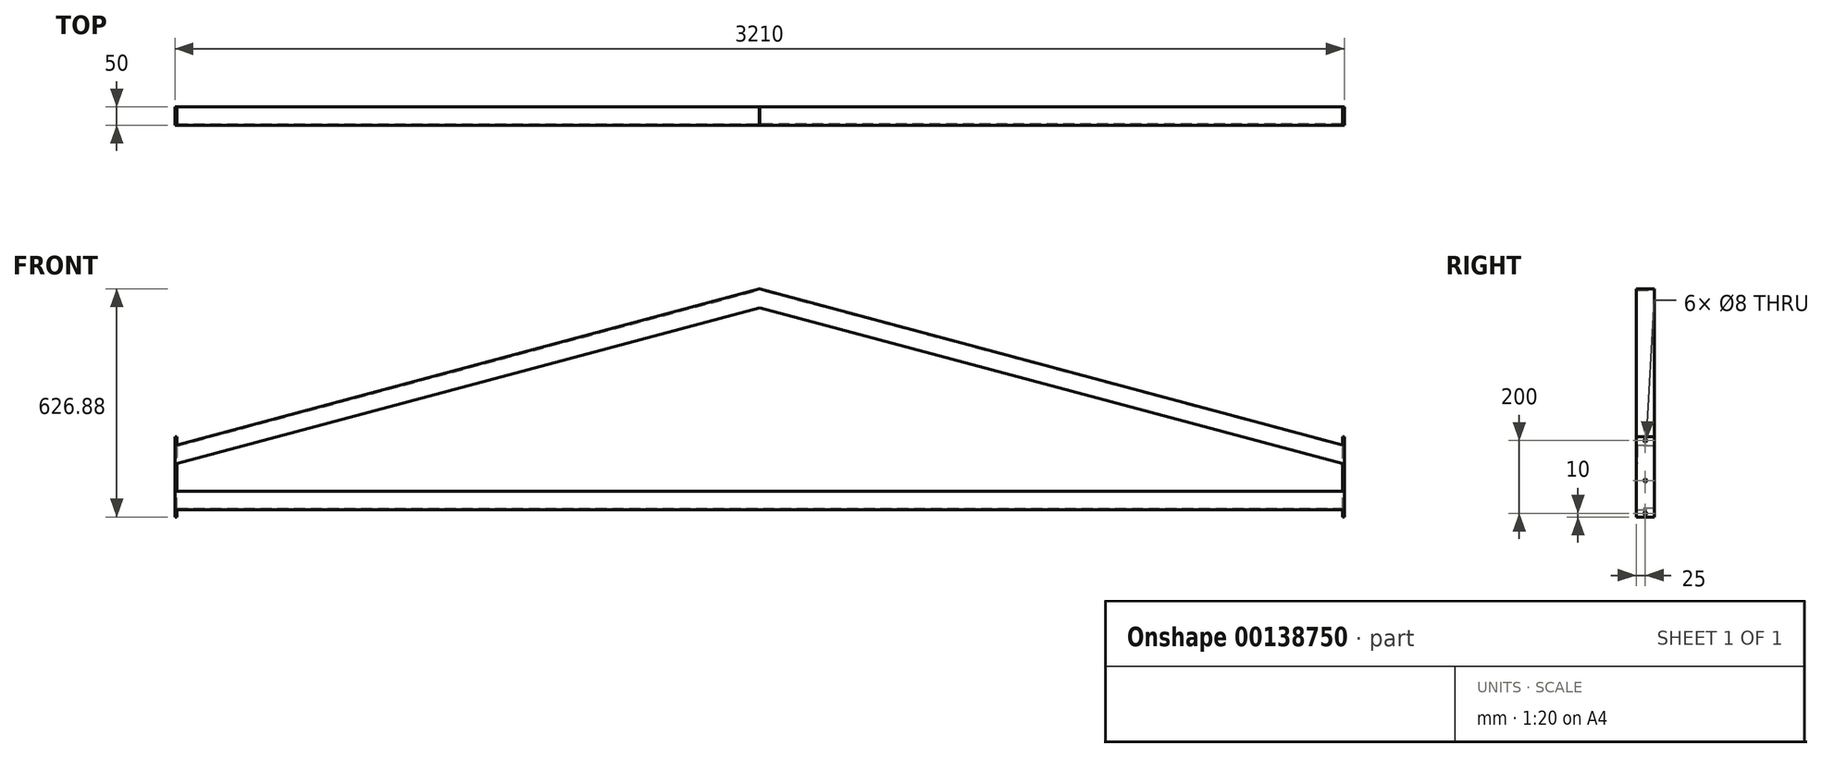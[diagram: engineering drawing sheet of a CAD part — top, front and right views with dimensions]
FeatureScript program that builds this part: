
annotation { "Feature Type Name" : "Feature", "Feature Type Description" : "" }
export const myFeature = defineFeature(function(context is Context, id is Id, definition is map)
    precondition{}
    {
        {
            var Q0;
            Q0=qCreatedBy(makeId("Right.planeOp"),FACE);
            var sketch = newSketch(context, id + "F0", { "sketchPlane" : qUnion([Q0])});
            skLineSegment(sketch, "E0", {"start": v(3, 50) * mm, "end": v(0, 50) * mm});
            skLineSegment(sketch, "E1", {"start": v(0, 50) * mm, "end": v(0, 0) * mm});
            skLineSegment(sketch, "E2", {"start": v(0, 0) * mm, "end": v(50, 0) * mm});
            skLineSegment(sketch, "E3", {"start": v(50, 0) * mm, "end": v(50, 3) * mm});
            skLineSegment(sketch, "E4", {"start": v(50, 3) * mm, "end": v(3, 3) * mm});
            skLineSegment(sketch, "E5", {"start": v(3, 3) * mm, "end": v(3, 50) * mm});
            skSolve(sketch);
        }
        {
            var Q0;
            Q0=qSketchRegion(id+"F0",true);
            extrude(context, id + "F1", {"entities" : qUnion([Q0]), "oppositeDirection" : true, "depth" : 1600 * mm});
        }
        {
            var Q0;
            Q0=qCreatedBy(makeId("Right.planeOp"),FACE);
            cPlane(context, id + "F2", {"entities" : qUnion([Q0]), "cplaneType" : CPlaneType.OFFSET, "offset" : 1600 * mm, "oppositeDirection" : true, "width" : 150 * mm, "height" : 150 * mm});
        }
        {
            var Q0;
            Q0=qCreatedBy(id+"F2.planeOp",FACE);
            var Q1;
            Q1=makeQuery(id+"F1.opExtrude","CAP_EDGE",EDGE,{"disambiguationData":[OSD([sQuery(id+"F0.wireOp",EDGE,"E2")])],"isStart":false});
            cPlane(context, id + "F3", {"entities" : qUnion([Q0, Q1]), "cplaneType" : CPlaneType.LINE_ANGLE, "offset" : 25 * mm, "angle" : 345 * degree, "width" : 150 * mm, "height" : 150 * mm});
        }
        {
            var Q0;
            Q0=qCreatedBy(id+"F2.planeOp",FACE);
            var sketch = newSketch(context, id + "F4", { "sketchPlane" : qUnion([Q0])});
            skLineSegment(sketch, "E6.bottom", {"start": v(50, -20) * mm, "end": v(0, -20) * mm});
            skLineSegment(sketch, "E6.top", {"start": v(50, 200) * mm, "end": v(0, 200) * mm});
            skLineSegment(sketch, "E6.left", {"start": v(50, -20) * mm, "end": v(50, 200) * mm});
            skLineSegment(sketch, "E6.right", {"start": v(0, -20) * mm, "end": v(0, 200) * mm});
            skSolve(sketch);
        }
        {
            var Q0;
            Q0=qSketchRegion(id+"F4",true);
            extrude(context, id + "F5", {"entities" : qUnion([Q0]), "operationType" : NewBodyOperationType.ADD, "oppositeDirection" : true, "depth" : 5 * mm});
        }
        {
            var Q0;
            Q0=qCreatedBy(id+"F3.planeOp",FACE);
            cPlane(context, id + "F6", {"entities" : qUnion([Q0]), "cplaneType" : CPlaneType.OFFSET, "offset" : 100 * mm, "oppositeDirection" : true, "width" : 150 * mm, "height" : 150 * mm});
        }
        {
            var Q0;
            Q0=qCreatedBy(id+"F6.planeOp",FACE);
            var sketch = newSketch(context, id + "F7", { "sketchPlane" : qUnion([Q0])});
            skLineSegment(sketch, "E7", {"start": v(-50, 586.09) * mm, "end": v(0, 586.09) * mm});
            skLineSegment(sketch, "E8", {"start": v(0, 586.09) * mm, "end": v(0, 536.09) * mm});
            skLineSegment(sketch, "E9", {"start": v(0, 536.09) * mm, "end": v(-3, 536.09) * mm});
            skLineSegment(sketch, "E10", {"start": v(-3, 536.09) * mm, "end": v(-3, 583.09) * mm});
            skLineSegment(sketch, "E11", {"start": v(-50, 583.09) * mm, "end": v(-50, 586.09) * mm});
            skLineSegment(sketch, "E12", {"start": v(-3, 583.09) * mm, "end": v(-50, 583.09) * mm});
            skSolve(sketch);
        }
        {
            var Q0;
            Q0=qSketchRegion(id+"F7",true);
            var Q1;
            {var subQ0=sQuery(id+"F4.wireOp",EDGE,"E6.right");var subQ1=sQuery(id+"F4.wireOp",EDGE,"E6.top");var subQ2=sQuery(id+"F4.wireOp",EDGE,"E6.left");Q1=makeQuery(id+"F5.boolean.opBoolean","SPLIT",FACE,{"disambiguationData":[TD([makeQuery(id+"F1.opExtrude","SWEPT_FACE",FACE,{"disambiguationData":[OSD([sQuery(id+"F0.wireOp",EDGE,"E0")])]})])],"derivedFrom":makeQuery(id+"F5.opExtrude","CAP_FACE",FACE,{"disambiguationData":[OSD([sQuery(id+"F4.wireOp",EDGE,"E6.bottom"),subQ1,subQ2,subQ0])],"isStart":true})});}
            var Q2;
            Q2=makeQuery(id+"FKIayfqTJtJaRCz_1.opExtrude","SWEPT_FACE",FACE,{"disambiguationData":[OSD([sQuery(id+"FGUrObEunJVsNxf_1.wireOp",EDGE,"07d030c4-0b13-4205-8b14-93d0722142eb.0")])]});
            extrude(context, id + "F8", {"entities" : qUnion([Q0]), "operationType" : NewBodyOperationType.ADD, "endBound" : BoundingType.UP_TO_SURFACE, "endBoundEntityFace" : qUnion([Q1]), "depth" : 25 * mm, "hasSecondDirection" : true, "secondDirectionOppositeDirection" : true, "secondDirectionBoundEntityFace" : qUnion([Q2]), "secondDirectionDepth" : 1603 * mm});
        }
        {
            var Q0;
            Q0=qCreatedBy(id+"F2.planeOp",FACE);
            var sketch = newSketch(context, id + "F9", { "sketchPlane" : qUnion([Q0])});
            skCircle(sketch, "E13", {"center": v(25, 190) * mm, "radius": 4 * mm});
            skCircle(sketch, "E14", {"center": v(25, 80) * mm, "radius": 4 * mm});
            skCircle(sketch, "E15", {"center": v(25, -10) * mm, "radius": 4 * mm});
            skSolve(sketch);
        }
        {
            var Q0;
            Q0=qSketchRegion(id+"F9",true);
            extrude(context, id + "F10", {"entities" : qUnion([Q0]), "operationType" : NewBodyOperationType.REMOVE, "oppositeDirection" : true, "depth" : 6 * mm});
        }
        {
            var Q0;
            Q0=makeQuery(id+"F1.opExtrude","SWEPT_BODY",BODY,{"disambiguationData":[OSD([sQuery(id+"F0.wireOp",EDGE,"E0"),sQuery(id+"F0.wireOp",EDGE,"E1"),sQuery(id+"F0.wireOp",EDGE,"E2"),sQuery(id+"F0.wireOp",EDGE,"E3"),sQuery(id+"F0.wireOp",EDGE,"E4"),sQuery(id+"F0.wireOp",EDGE,"E5")])]});
            var Q1;
            Q1=qCreatedBy(makeId("Right.planeOp"),FACE);
            mirror(context, id + "F11", {"operationType" : NewBodyOperationType.ADD, "entities" : qUnion([Q0]), "mirrorPlane" : qUnion([Q1])});
        }
    });
